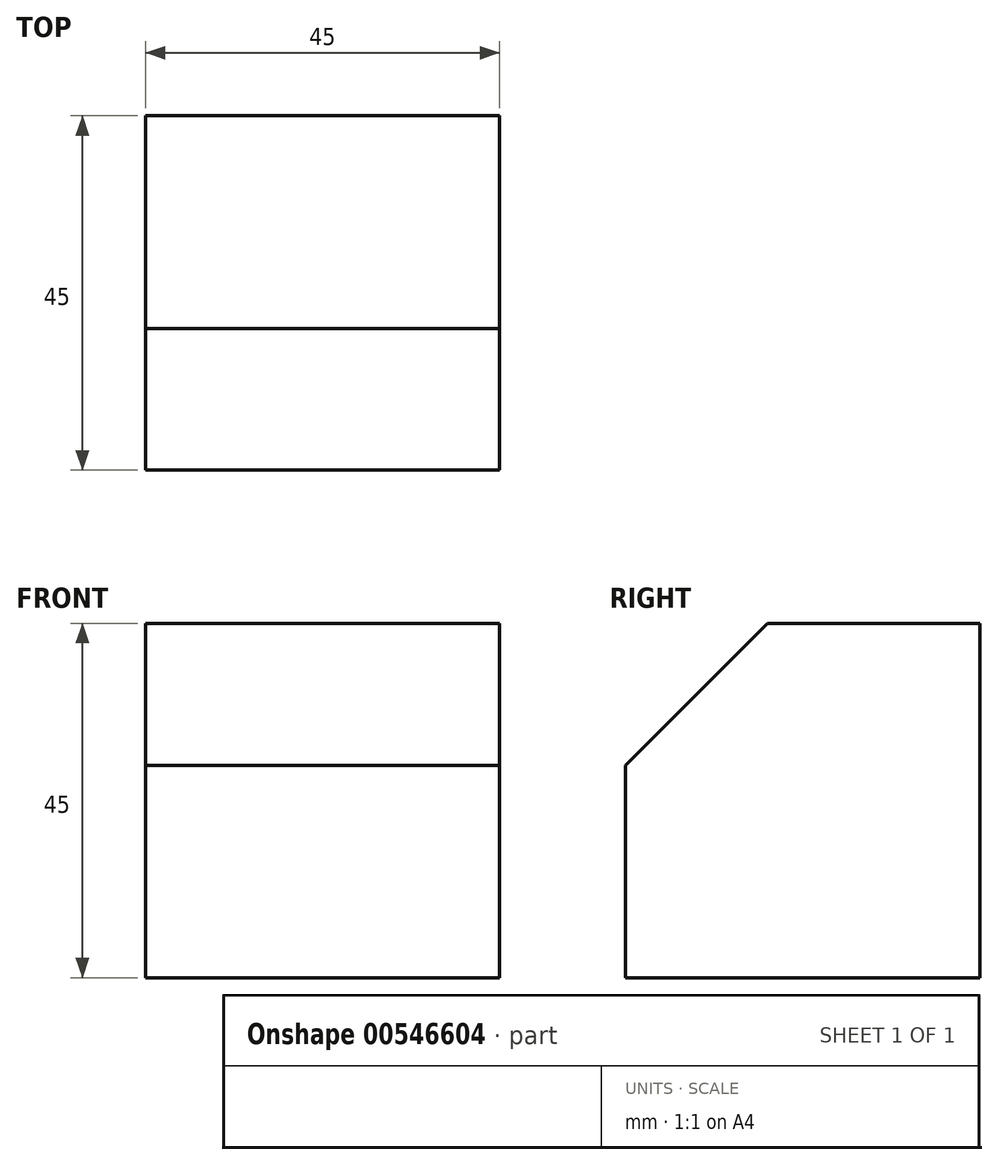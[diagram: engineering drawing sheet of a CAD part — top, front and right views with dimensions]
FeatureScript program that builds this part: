
annotation { "Feature Type Name" : "Feature", "Feature Type Description" : "" }
export const myFeature = defineFeature(function(context is Context, id is Id, definition is map)
    precondition{}
    {
        {
            var Q0;
            Q0=qCreatedBy(makeId("Top.planeOp"),FACE);
            var sketch = newSketch(context, id + "F0", { "sketchPlane" : qUnion([Q0])});
            skLineSegment(sketch, "E0.bottom", {"start": v(0, 45) * mm, "end": v(45, 45) * mm});
            skLineSegment(sketch, "E0.top", {"start": v(0, 0) * mm, "end": v(45, 0) * mm});
            skLineSegment(sketch, "E0.left", {"start": v(0, 45) * mm, "end": v(0, 0) * mm});
            skLineSegment(sketch, "E0.right", {"start": v(45, 45) * mm, "end": v(45, 0) * mm});
            skSolve(sketch);
        }
        {
            var Q0;
            Q0=makeQuery(id+"F0.imprint","IMPRINT",FACE,{"disambiguationData":[TD([[makeQuery(id+"F0.imprint","IMPRINT",EDGE,{"derivedFrom":sQuery(id+"F0.wireOp",EDGE,"E0.bottom")}),-1.0]])]});
            extrude(context, id + "F1", {"entities" : qUnion([Q0]), "depth" : 45 * mm, "offsetDistance" : 25 * mm});
        }
        {
            var Q0;
            Q0=makeQuery(id+"F1.opExtrude","CAP_EDGE",EDGE,{"disambiguationData":[OSD([sQuery(id+"F0.wireOp",EDGE,"E0.top")])],"isStart":false});
            chamfer(context, id + "F2", {"entities" : qUnion([Q0]), "width" : 18 * mm, "tangentPropagation" : true});
        }
    });
